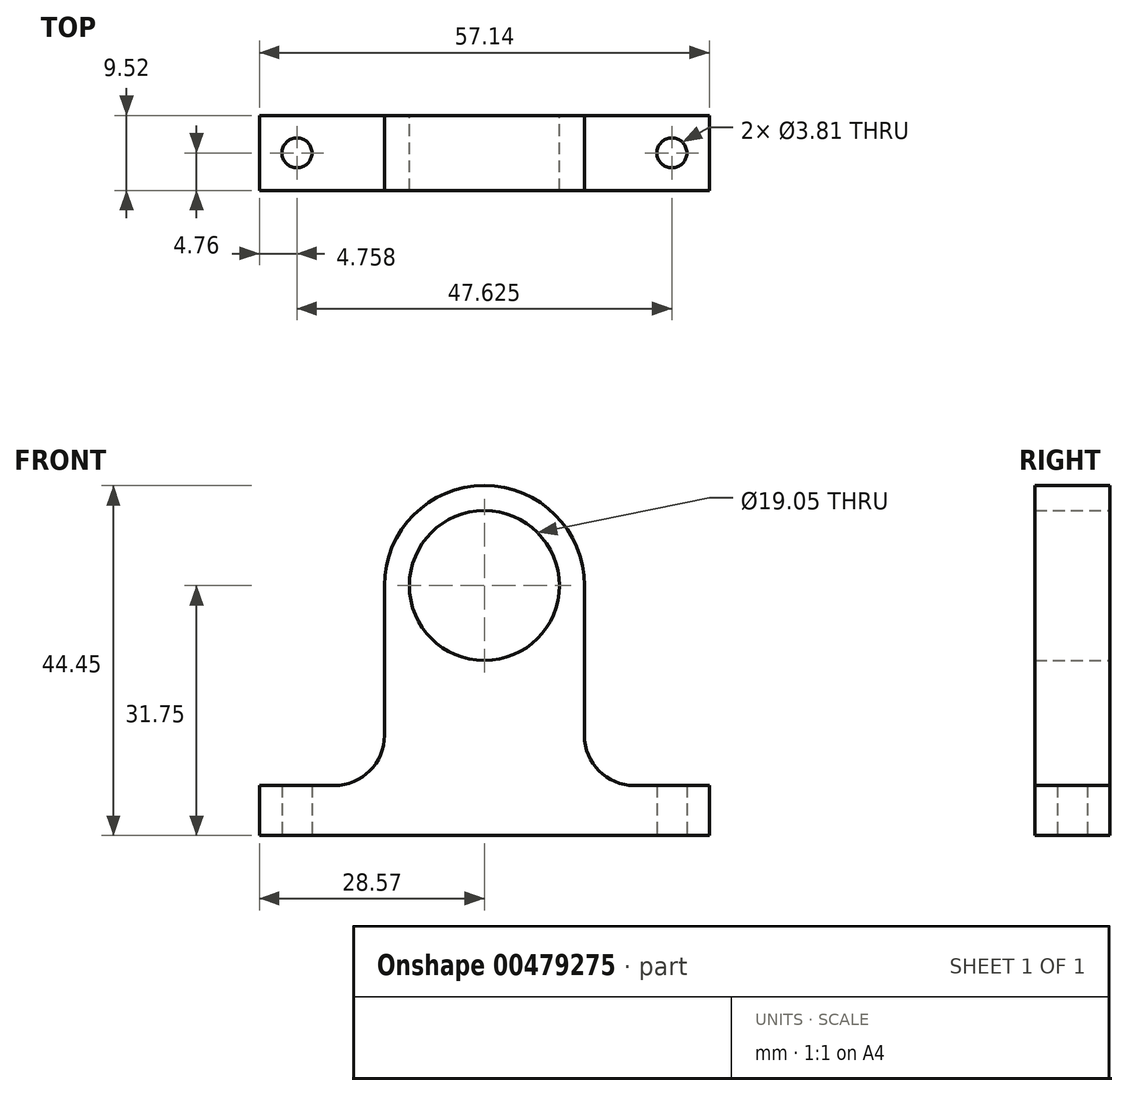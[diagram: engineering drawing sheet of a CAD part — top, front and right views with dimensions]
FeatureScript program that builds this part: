
annotation { "Feature Type Name" : "Feature", "Feature Type Description" : "" }
export const myFeature = defineFeature(function(context is Context, id is Id, definition is map)
    precondition{}
    {
        {
            var Q0;
            Q0=qCreatedBy(makeId("Front.planeOp"),FACE);
            var sketch = newSketch(context, id + "F0", { "sketchPlane" : qUnion([Q0])});
            skCircle(sketch, "E0", {"center": v(0, 0) * mm, "radius": 9.53 * mm});
            skArc(sketch, "E1", {"start": v(12.7, 0) * mm, "mid": v(0, 12.7) * mm, "end": v(-12.7, 0) * mm});
            skLineSegment(sketch, "E2", {"start": v(-12.7, 0) * mm, "end": v(-12.7, -25.4) * mm});
            skLineSegment(sketch, "E3", {"start": v(-12.7, -25.4) * mm, "end": v(-28.57, -25.4) * mm});
            skLineSegment(sketch, "E4", {"start": v(-28.58, -25.4) * mm, "end": v(-28.58, -31.75) * mm});
            skLineSegment(sketch, "E5", {"start": v(-28.58, -31.75) * mm, "end": v(28.57, -31.75) * mm});
            skLineSegment(sketch, "E6", {"start": v(28.57, -31.75) * mm, "end": v(28.57, -25.4) * mm});
            skLineSegment(sketch, "E7", {"start": v(28.57, -25.4) * mm, "end": v(12.7, -25.4) * mm});
            skLineSegment(sketch, "E8", {"start": v(12.7, -25.4) * mm, "end": v(12.7, 0) * mm});
            skSolve(sketch);
        }
        {
            var Q0;
            Q0=makeQuery(id+"F0.imprint","IMPRINT",FACE,{"disambiguationData":[TD([[makeQuery(id+"F0.imprint","IMPRINT",EDGE,{"derivedFrom":sQuery(id+"F0.wireOp",EDGE,"E0")}),-1.0]])]});
            extrude(context, id + "F1", {"entities" : qUnion([Q0]), "endBound" : BoundingType.SYMMETRIC, "depth" : 9.52 * mm});
        }
        {
            var Q0;
            Q0=makeQuery(id+"F1.opExtrude","SWEPT_EDGE",EDGE,{"disambiguationData":[OSD([sQuery(id+"F0.wireOp",EDGE,"E2"),sQuery(id+"F0.wireOp",EDGE,"E3")])]});
            var Q1;
            Q1=makeQuery(id+"F1.opExtrude","SWEPT_EDGE",EDGE,{"disambiguationData":[OSD([sQuery(id+"F0.wireOp",EDGE,"E7"),sQuery(id+"F0.wireOp",EDGE,"E8")])]});
            fillet(context, id + "F2", {"entities" : qUnion([Q0, Q1]), "radius" : 6.35 * mm, "tangentPropagation" : true, "allowEdgeOverflow" : false});
        }
        {
            var Q0;
            Q0=makeQuery(id+"F1.opExtrude","SWEPT_FACE",FACE,{"disambiguationData":[OSD([sQuery(id+"F0.wireOp",EDGE,"E5")])]});
            var sketch = newSketch(context, id + "F3", { "sketchPlane" : qUnion([Q0])});
            skCircle(sketch, "E9", {"center": v(-23.81, 0) * mm, "radius": 1.87 * mm});
            skCircle(sketch, "E10", {"center": v(23.81, 0) * mm, "radius": 1.83 * mm});
            skSolve(sketch);
        }
        {
            var Q0;
            Q0=sQuery(id+"F3.wireOp",VERTEX,"E9.center");
            var Q1;
            Q1=sQuery(id+"F3.wireOp",VERTEX,"E10.center");
            var Q2;
            Q2=makeQuery(id+"F1.opExtrude","SWEPT_BODY",BODY,{"disambiguationData":[OSD([sQuery(id+"F0.wireOp",EDGE,"E0"),sQuery(id+"F0.wireOp",EDGE,"E1"),sQuery(id+"F0.wireOp",EDGE,"E2"),sQuery(id+"F0.wireOp",EDGE,"E3"),sQuery(id+"F0.wireOp",EDGE,"E4"),sQuery(id+"F0.wireOp",EDGE,"E5"),sQuery(id+"F0.wireOp",EDGE,"E6"),sQuery(id+"F0.wireOp",EDGE,"E7"),sQuery(id+"F0.wireOp",EDGE,"E8")])]});
            hole(context, id + "F4", {"style" : HoleStyle.SIMPLE, "endStyle" : HoleEndStyle.THROUGH, "holeDiameter" : 3.8 * mm, "locations" : qUnion([Q0, Q1]), "scope" : qUnion([Q2]), "tappedDepth" : 12.7 * mm, "tapClearance" : 3});
        }
    });
